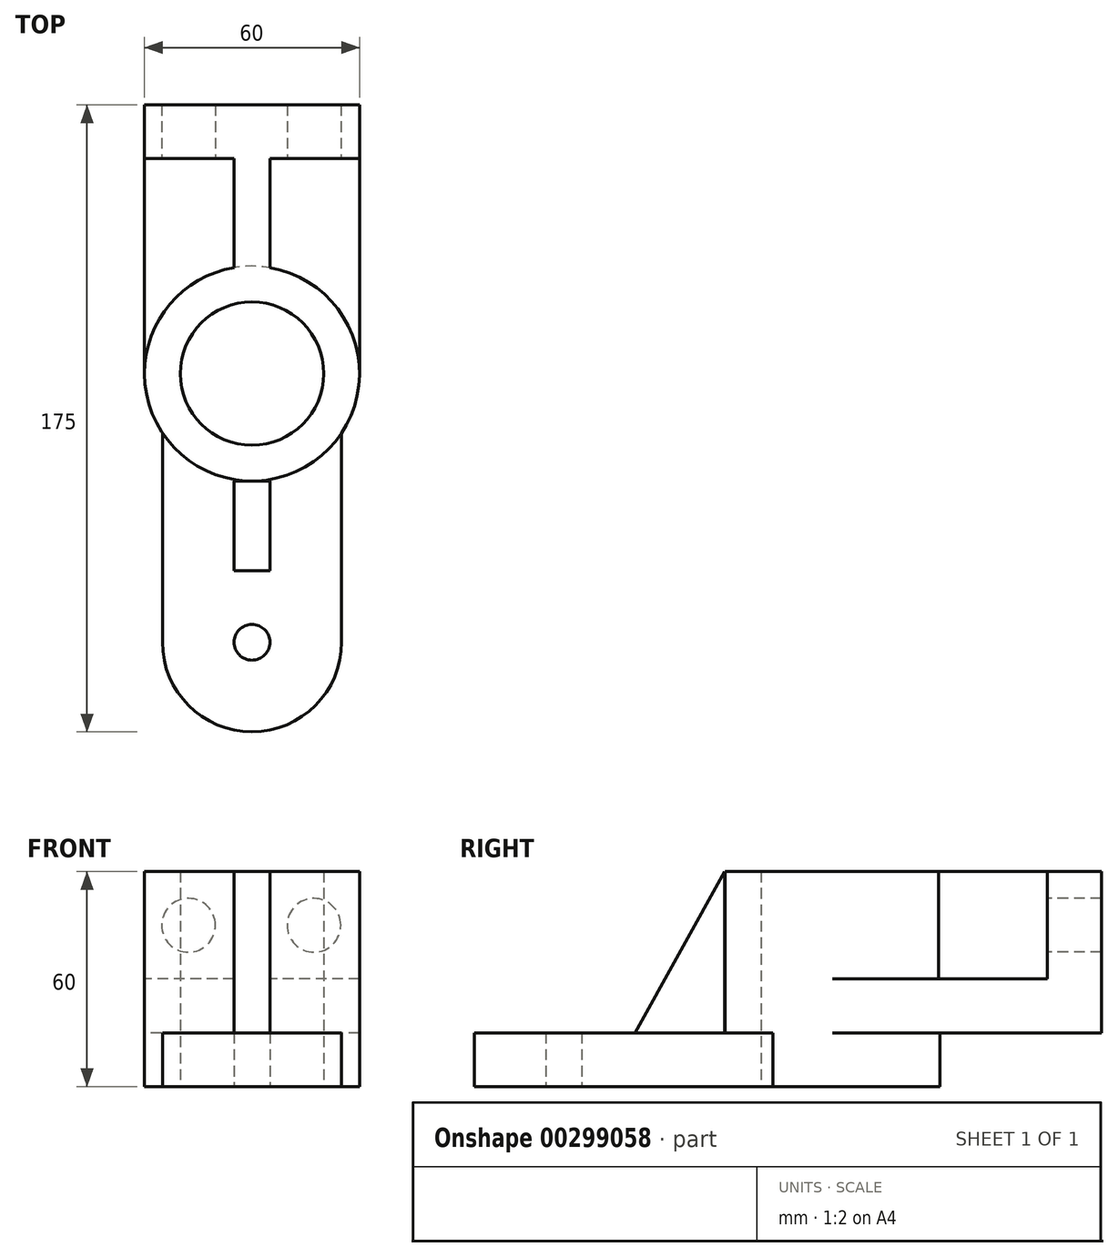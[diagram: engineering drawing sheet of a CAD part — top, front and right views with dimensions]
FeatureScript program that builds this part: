
annotation { "Feature Type Name" : "Feature", "Feature Type Description" : "" }
export const myFeature = defineFeature(function(context is Context, id is Id, definition is map)
    precondition{}
    {
        {
            var Q0;
            Q0=qCreatedBy(makeId("Top.planeOp"),FACE);
            var sketch = newSketch(context, id + "F0", { "sketchPlane" : qUnion([Q0])});
            skCircle(sketch, "E0", {"center": v(0, 0) * mm, "radius": 20 * mm});
            skCircle(sketch, "E1", {"center": v(0, 0) * mm, "radius": 30 * mm});
            skLineSegment(sketch, "E2", {"start": v(-30, 75) * mm, "end": v(-30, 75) * mm});
            skLineSegment(sketch, "E3", {"start": v(30, 75) * mm, "end": v(30, 60) * mm});
            skLineSegment(sketch, "E4", {"start": v(30, 60) * mm, "end": v(5, 60) * mm});
            skLineSegment(sketch, "E5", {"start": v(5, 60) * mm, "end": v(5, 29.58) * mm});
            skLineSegment(sketch, "E6", {"start": v(-30, 75) * mm, "end": v(-30, 0) * mm});
            skLineSegment(sketch, "E7", {"start": v(30, 60) * mm, "end": v(30, 0) * mm});
            skLineSegment(sketch, "E8", {"start": v(-30, 75) * mm, "end": v(30, 75) * mm});
            skLineSegment(sketch, "E9", {"start": v(-5, 29.58) * mm, "end": v(-5, 60) * mm});
            skLineSegment(sketch, "E10", {"start": v(-5, 60) * mm, "end": v(-30, 60) * mm});
            skCircle(sketch, "E11", {"center": v(0, -75) * mm, "radius": 5 * mm});
            skLineSegment(sketch, "E12", {"start": v(-25, -16.58) * mm, "end": v(-25, -75) * mm});
            skArc(sketch, "E13", {"start": v(-25, -75) * mm, "mid": v(0, -100) * mm, "end": v(25, -75) * mm});
            skLineSegment(sketch, "E14", {"start": v(25, -75) * mm, "end": v(25, -16.58) * mm});
            skLineSegment(sketch, "E15", {"start": v(-5, -54.58) * mm, "end": v(0, -54.58) * mm});
            skLineSegment(sketch, "E16", {"start": v(0, -54.58) * mm, "end": v(5, -54.58) * mm});
            skLineSegment(sketch, "E17", {"start": v(5, -54.58) * mm, "end": v(5, -29.58) * mm});
            skLineSegment(sketch, "E18", {"start": v(-5, -54.58) * mm, "end": v(-5, -29.58) * mm});
            skSolve(sketch);
        }
        {
            var Q0;
            Q0=makeQuery(id+"F0.imprint","IMPRINT",FACE,{"disambiguationData":[TD([[makeQuery(id+"F0.imprint","IMPRINT",EDGE,{"derivedFrom":sQuery(id+"F0.wireOp",EDGE,"E0")}),-1.0]])]});
            extrude(context, id + "F1", {"entities" : qUnion([Q0]), "depth" : 60 * mm});
        }
        {
            var Q0;
            Q0=makeQuery(id+"F0.imprint","IMPRINT",FACE,{"disambiguationData":[TD([[makeQuery(id+"F0.imprint","IMPRINT",EDGE,{"derivedFrom":sQuery(id+"F0.wireOp",EDGE,"E11")}),-1.0]])]});
            var Q1;
            Q1=makeQuery(id+"F0.imprint","IMPRINT",FACE,{"disambiguationData":[TD([[makeQuery(id+"F0.imprint","IMPRINT",EDGE,{"derivedFrom":sQuery(id+"F0.wireOp",EDGE,"E15")}),1.0]])]});
            extrude(context, id + "F2", {"entities" : qUnion([Q0, Q1]), "operationType" : NewBodyOperationType.ADD, "depth" : 15 * mm});
        }
        {
            var Q0;
            {var subQ3=sQuery(id+"F0.wireOp",EDGE,"E9");Q0=makeQuery(id+"F0.imprint","IMPRINT",FACE,{"disambiguationData":[TD([[makeQuery(id+"F0.imprint","IMPRINT",EDGE,{"derivedFrom":subQ3}),1.0]])]});}
            var Q1;
            Q1=makeQuery(id+"F0.imprint","IMPRINT",FACE,{"disambiguationData":[TD([[makeQuery(id+"F0.imprint","IMPRINT",EDGE,{"derivedFrom":sQuery(id+"F0.wireOp",EDGE,"E3")}),-1.0]])]});
            var Q2;
            Q2=makeQuery(id+"F0.imprint","IMPRINT",FACE,{"disambiguationData":[TD([[makeQuery(id+"F0.imprint","IMPRINT",EDGE,{"derivedFrom":sQuery(id+"F0.wireOp",EDGE,"E4")}),1.0]])]});
            extrude(context, id + "F3", {"entities" : qUnion([Q0, Q1, Q2]), "operationType" : NewBodyOperationType.ADD, "depth" : 60 * mm});
        }
        {
            var Q0;
            Q0=makeQuery(id+"F0.imprint","IMPRINT",FACE,{"disambiguationData":[TD([[makeQuery(id+"F0.imprint","IMPRINT",EDGE,{"derivedFrom":sQuery(id+"F0.wireOp",EDGE,"E3")}),-1.0]])]});
            extrude(context, id + "F4", {"entities" : qUnion([Q0]), "operationType" : NewBodyOperationType.ADD, "depth" : 45 * mm});
        }
        {
            var Q0;
            {var subQ3=sQuery(id+"F0.wireOp",EDGE,"E9");Q0=makeQuery(id+"F0.imprint","IMPRINT",FACE,{"disambiguationData":[TD([[makeQuery(id+"F0.imprint","IMPRINT",EDGE,{"derivedFrom":subQ3}),1.0]])]});}
            var Q1;
            Q1=makeQuery(id+"F0.imprint","IMPRINT",FACE,{"disambiguationData":[TD([[makeQuery(id+"F0.imprint","IMPRINT",EDGE,{"derivedFrom":sQuery(id+"F0.wireOp",EDGE,"E3")}),-1.0]])]});
            var Q2;
            Q2=makeQuery(id+"F0.imprint","IMPRINT",FACE,{"disambiguationData":[TD([[makeQuery(id+"F0.imprint","IMPRINT",EDGE,{"derivedFrom":sQuery(id+"F0.wireOp",EDGE,"E4")}),1.0]])]});
            extrude(context, id + "F5", {"entities" : qUnion([Q0, Q1, Q2]), "operationType" : NewBodyOperationType.REMOVE, "depth" : 15 * mm});
        }
        {
            var Q0;
            {var subQ0=sQuery(id+"F0.wireOp",EDGE,"E1");Q0=makeQuery(id+"F3.boolean.opBoolean","MERGE",FACE,{"derivedFrom":[makeQuery(id+"F1.opExtrude","CAP_FACE",FACE,{"disambiguationData":[OSD([sQuery(id+"F0.wireOp",EDGE,"E0"),subQ0])],"isStart":false}),makeQuery(id+"F3.opExtrude","CAP_FACE",FACE,{"disambiguationData":[OSD([subQ0,sQuery(id+"F0.wireOp",EDGE,"E3"),sQuery(id+"F0.wireOp",EDGE,"E6"),sQuery(id+"F0.wireOp",EDGE,"E7"),sQuery(id+"F0.wireOp",EDGE,"E8")])],"isStart":false})]});}
            var sketch = newSketch(context, id + "F6", { "sketchPlane" : qUnion([Q0])});
            skLineSegment(sketch, "E19.0", {"start": v(-5, 60) * mm, "end": v(-30, 60) * mm});
            skLineSegment(sketch, "E19.1", {"start": v(-5, 29.58) * mm, "end": v(-5, 60) * mm});
            skLineSegment(sketch, "E19.2", {"start": v(-30, 75) * mm, "end": v(-30, 0) * mm});
            skCircle(sketch, "E19.3", {"center": v(0, 0) * mm, "radius": 30 * mm});
            skLineSegment(sketch, "E19.4", {"start": v(5, 60) * mm, "end": v(5, 29.58) * mm});
            skLineSegment(sketch, "E19.5", {"start": v(30, 60) * mm, "end": v(5, 60) * mm});
            skLineSegment(sketch, "E19.6", {"start": v(30, 60) * mm, "end": v(30, 0) * mm});
            skLineSegment(sketch, "E19.7", {"start": v(-30, 75) * mm, "end": v(30, 75) * mm});
            skLineSegment(sketch, "E19.8", {"start": v(30, 75) * mm, "end": v(30, 60) * mm});
            skSolve(sketch);
        }
        {
            var Q0;
            {var subQ0=sQuery(id+"F6.wireOp",EDGE,"E19.0");Q0=makeQuery(id+"F6.imprint","IMPRINT",FACE,{"disambiguationData":[TD([[makeQuery(id+"F6.imprint","IMPRINT",EDGE,{"derivedFrom":subQ0}),1.0]])]});}
            var Q1;
            {var subQ2=sQuery(id+"F6.wireOp",EDGE,"E19.4");Q1=makeQuery(id+"F6.imprint","IMPRINT",FACE,{"disambiguationData":[TD([[makeQuery(id+"F6.imprint","IMPRINT",EDGE,{"derivedFrom":subQ2}),1.0]])]});}
            extrude(context, id + "F7", {"entities" : qUnion([Q0, Q1]), "operationType" : NewBodyOperationType.REMOVE, "oppositeDirection" : true, "depth" : 30 * mm});
        }
        {
            var Q0;
            Q0=qCreatedBy(makeId("Right.planeOp"),FACE);
            var sketch = newSketch(context, id + "F8", { "sketchPlane" : qUnion([Q0])});
            skLineSegment(sketch, "E20", {"start": v(-30.07, 15) * mm, "end": v(-30.07, 60) * mm});
            skLineSegment(sketch, "E21", {"start": v(-30.07, 60) * mm, "end": v(-55.07, 15) * mm});
            skLineSegment(sketch, "E22", {"start": v(-30.07, 15) * mm, "end": v(-55.07, 15) * mm});
            skSolve(sketch);
        }
        {
            var Q0;
            Q0=makeQuery(id+"F8.imprint","IMPRINT",FACE,{"disambiguationData":[TD([[makeQuery(id+"F8.imprint","IMPRINT",EDGE,{"derivedFrom":sQuery(id+"F8.wireOp",EDGE,"E20")}),1.0]])]});
            extrude(context, id + "F9", {"entities" : qUnion([Q0]), "operationType" : NewBodyOperationType.ADD, "endBound" : BoundingType.SYMMETRIC, "depth" : 10 * mm});
        }
        {
            var Q0;
            Q0=makeQuery(id+"F7.boolean.opBoolean","COPY",FACE,{"derivedFrom":makeQuery(id+"F7.opExtrude","SWEPT_FACE",FACE,{"disambiguationData":[OSD([sQuery(id+"F6.wireOp",EDGE,"E19.0")])]})});
            var sketch = newSketch(context, id + "F10", { "sketchPlane" : qUnion([Q0])});
            skLineSegment(sketch, "E23.0", {"start": v(-5, 60) * mm, "end": v(-30, 60) * mm});
            skCircle(sketch, "E24", {"center": v(-17.71, 45) * mm, "radius": 7.5 * mm});
            skCircle(sketch, "E25", {"center": v(17.29, 45) * mm, "radius": 7.5 * mm});
            skLineSegment(sketch, "E26.0", {"start": v(30, 60) * mm, "end": v(5, 60) * mm});
            skSolve(sketch);
        }
        {
            var Q0;
            Q0=makeQuery(id+"F10.imprint","IMPRINT",FACE,{"disambiguationData":[TD([[makeQuery(id+"F10.imprint","IMPRINT",EDGE,{"derivedFrom":sQuery(id+"F10.wireOp",EDGE,"E24")}),1.0]])]});
            var Q1;
            Q1=makeQuery(id+"F10.imprint","IMPRINT",FACE,{"disambiguationData":[TD([[makeQuery(id+"F10.imprint","IMPRINT",EDGE,{"derivedFrom":sQuery(id+"F10.wireOp",EDGE,"E25")}),1.0]])]});
            extrude(context, id + "F11", {"entities" : qUnion([Q0, Q1]), "operationType" : NewBodyOperationType.REMOVE, "oppositeDirection" : true, "depth" : 15 * mm});
        }
    });
